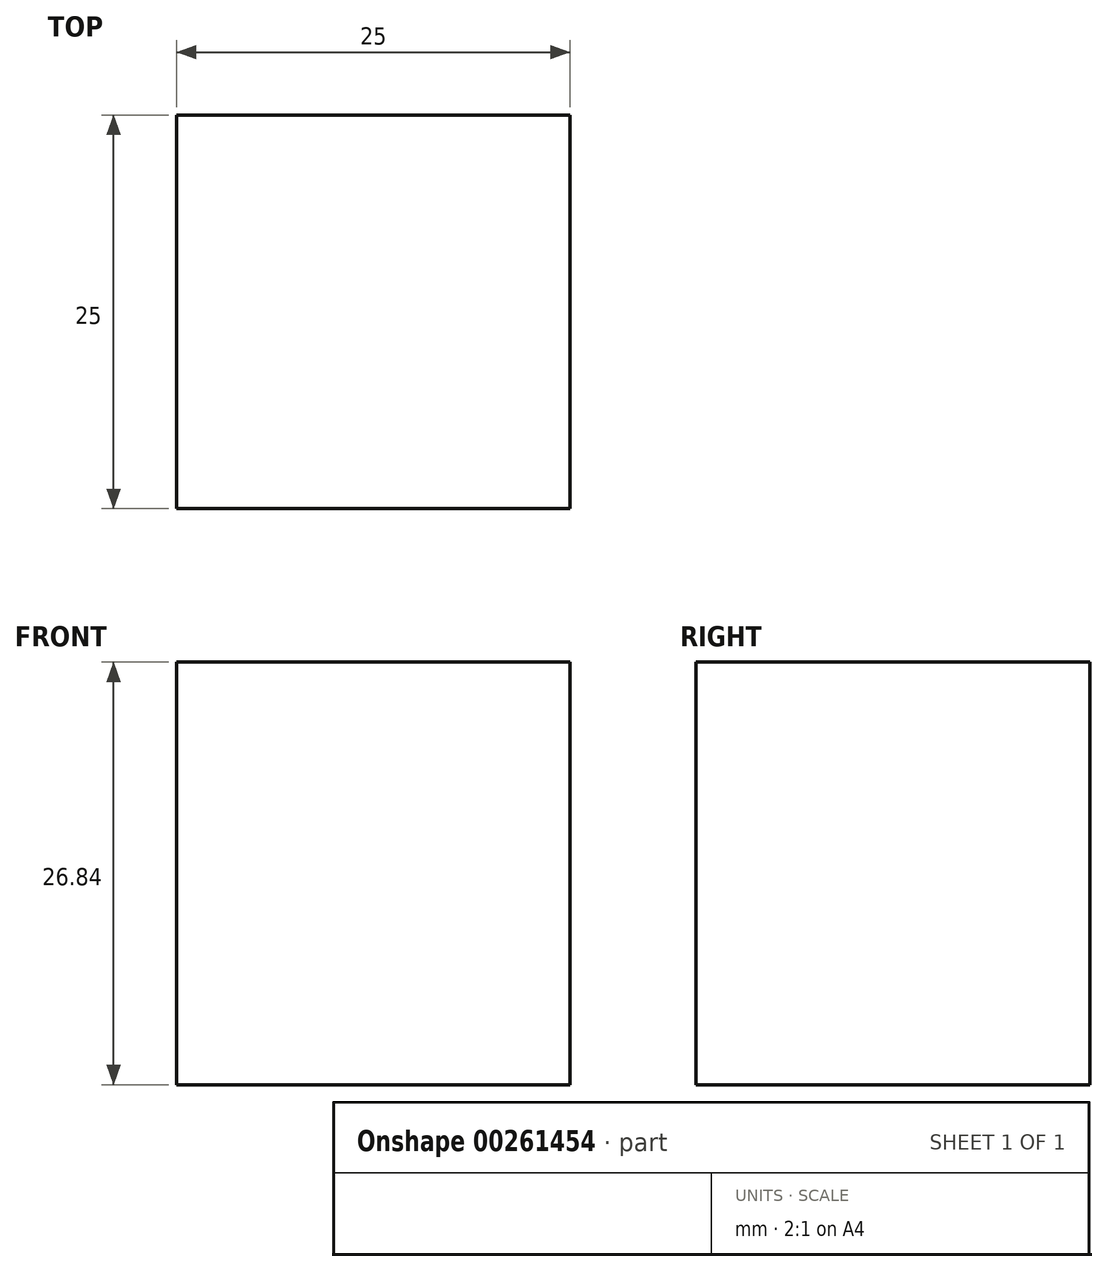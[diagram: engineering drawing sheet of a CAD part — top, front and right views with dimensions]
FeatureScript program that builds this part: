
annotation { "Feature Type Name" : "Feature", "Feature Type Description" : "" }
export const myFeature = defineFeature(function(context is Context, id is Id, definition is map)
    precondition{}
    {
        {
            var Q0;
            Q0=qCreatedBy(makeId("Front.planeOp"),FACE);
            var sketch = newSketch(context, id + "F0", { "sketchPlane" : qUnion([Q0])});
            skLineSegment(sketch, "E0.bottom", {"start": v(12.5, -13.42) * mm, "end": v(-12.5, -13.42) * mm});
            skLineSegment(sketch, "E0.top", {"start": v(12.5, 13.42) * mm, "end": v(-12.5, 13.42) * mm});
            skLineSegment(sketch, "E0.left", {"start": v(12.5, -13.42) * mm, "end": v(12.5, 13.42) * mm});
            skLineSegment(sketch, "E0.right", {"start": v(-12.5, -13.42) * mm, "end": v(-12.5, 13.42) * mm});
            skPoint(sketch, "E0.middle", {"position": v(0, 0) * mm});
            skSolve(sketch);
        }
        {
            var Q0;
            Q0=makeQuery(id+"F0.imprint","IMPRINT",FACE,{"disambiguationData":[TD([[makeQuery(id+"F0.imprint","IMPRINT",EDGE,{"derivedFrom":sQuery(id+"F0.wireOp",EDGE,"E0.bottom")}),-1.0]])]});
            extrude(context, id + "F1", {"entities" : qUnion([Q0]), "depth" : 25 * mm});
        }
    });
